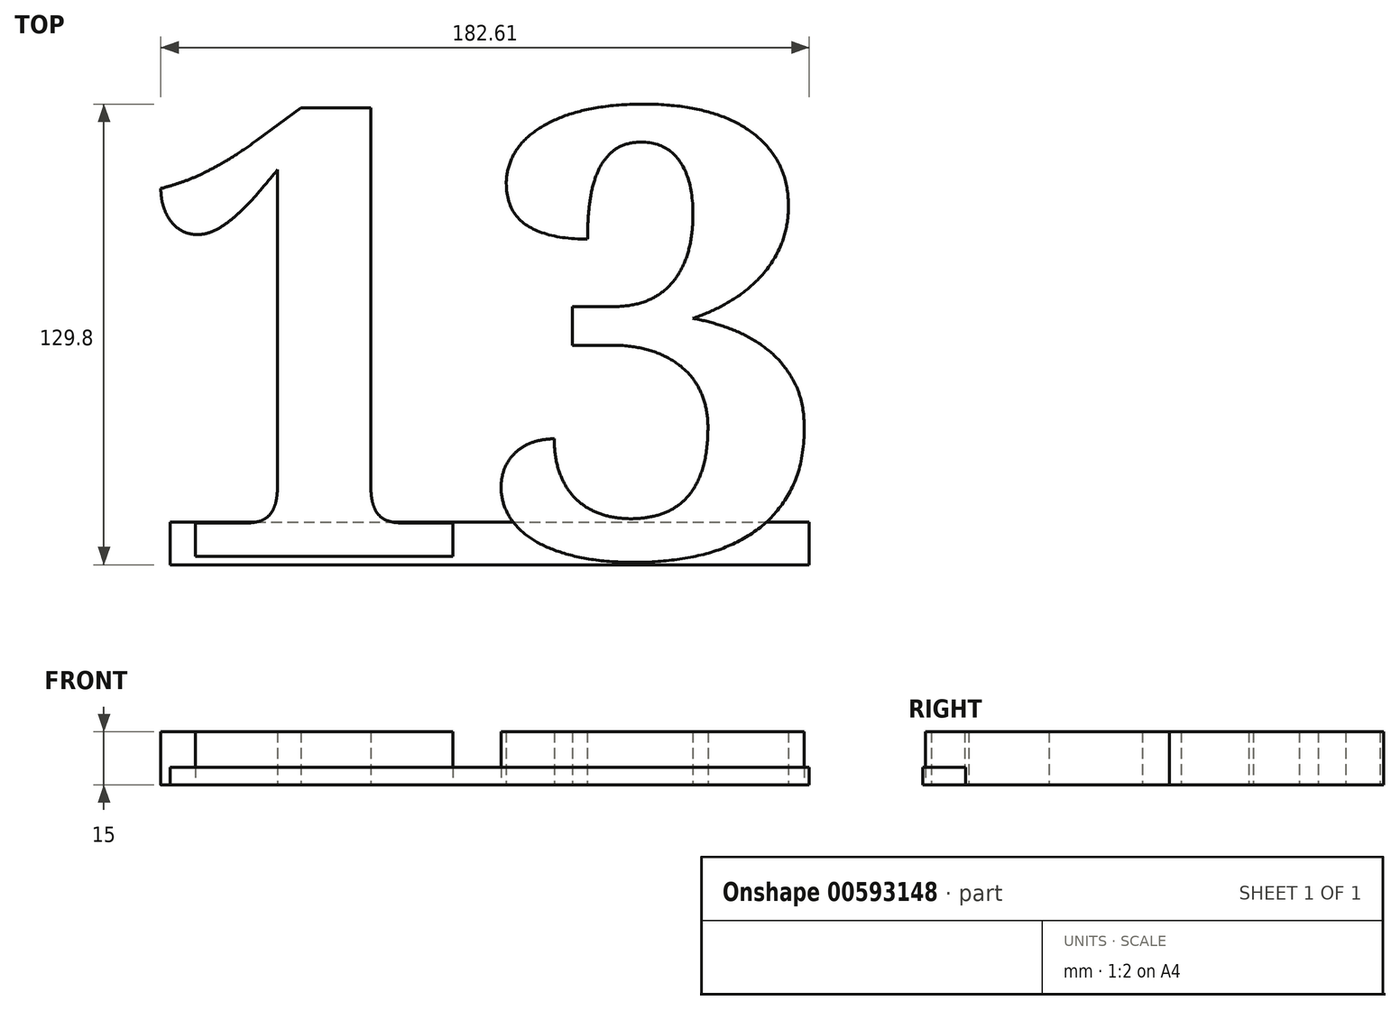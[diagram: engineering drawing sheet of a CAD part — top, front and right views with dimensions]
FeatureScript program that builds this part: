
annotation { "Feature Type Name" : "Feature", "Feature Type Description" : "" }
export const myFeature = defineFeature(function(context is Context, id is Id, definition is map)
    precondition{}
    {
        {
            var Q0;
            Q0=qCreatedBy(makeId("Top.planeOp"),FACE);
            var sketch = newSketch(context, id + "F0", { "sketchPlane" : qUnion([Q0])});
            skText(sketch, "E0", { "text": "13", "fontName": "NotoSerif-Bold.ttf"});
            const initialGuessF0  = {"E0": [-0.1, -0.06347, 1, 0, 0.12665]};
            skSetInitialGuess(sketch, initialGuessF0);
            skSolve(sketch);
        }
        {
            var Q0;
            Q0 = qSketchRegion(id + "F0", true);
            extrude(context, id + "F1", {"entities" : qUnion([Q0]), "depth" : 15 * mm, "offsetDistance" : 25 * mm});
        }
        {
            var Q0;
            Q0=qCreatedBy(makeId("Top.planeOp"),FACE);
            var sketch = newSketch(context, id + "F2", { "sketchPlane" : qUnion([Q0])});
            skLineSegment(sketch, "E1.bottom", {"start": v(-90, -53.91) * mm, "end": v(90, -53.91) * mm});
            skLineSegment(sketch, "E1.top", {"start": v(-90, -65.91) * mm, "end": v(90, -65.91) * mm});
            skLineSegment(sketch, "E1.left", {"start": v(-90, -53.91) * mm, "end": v(-90, -65.91) * mm});
            skLineSegment(sketch, "E1.right", {"start": v(90, -53.91) * mm, "end": v(90, -65.91) * mm});
            skSolve(sketch);
        }
        {
            var Q0;
            Q0 = qSketchRegion(id + "F2", true);
            extrude(context, id + "F3", {"entities" : qUnion([Q0]), "depth" : 5 * mm, "offsetDistance" : 25 * mm});
        }
    });
